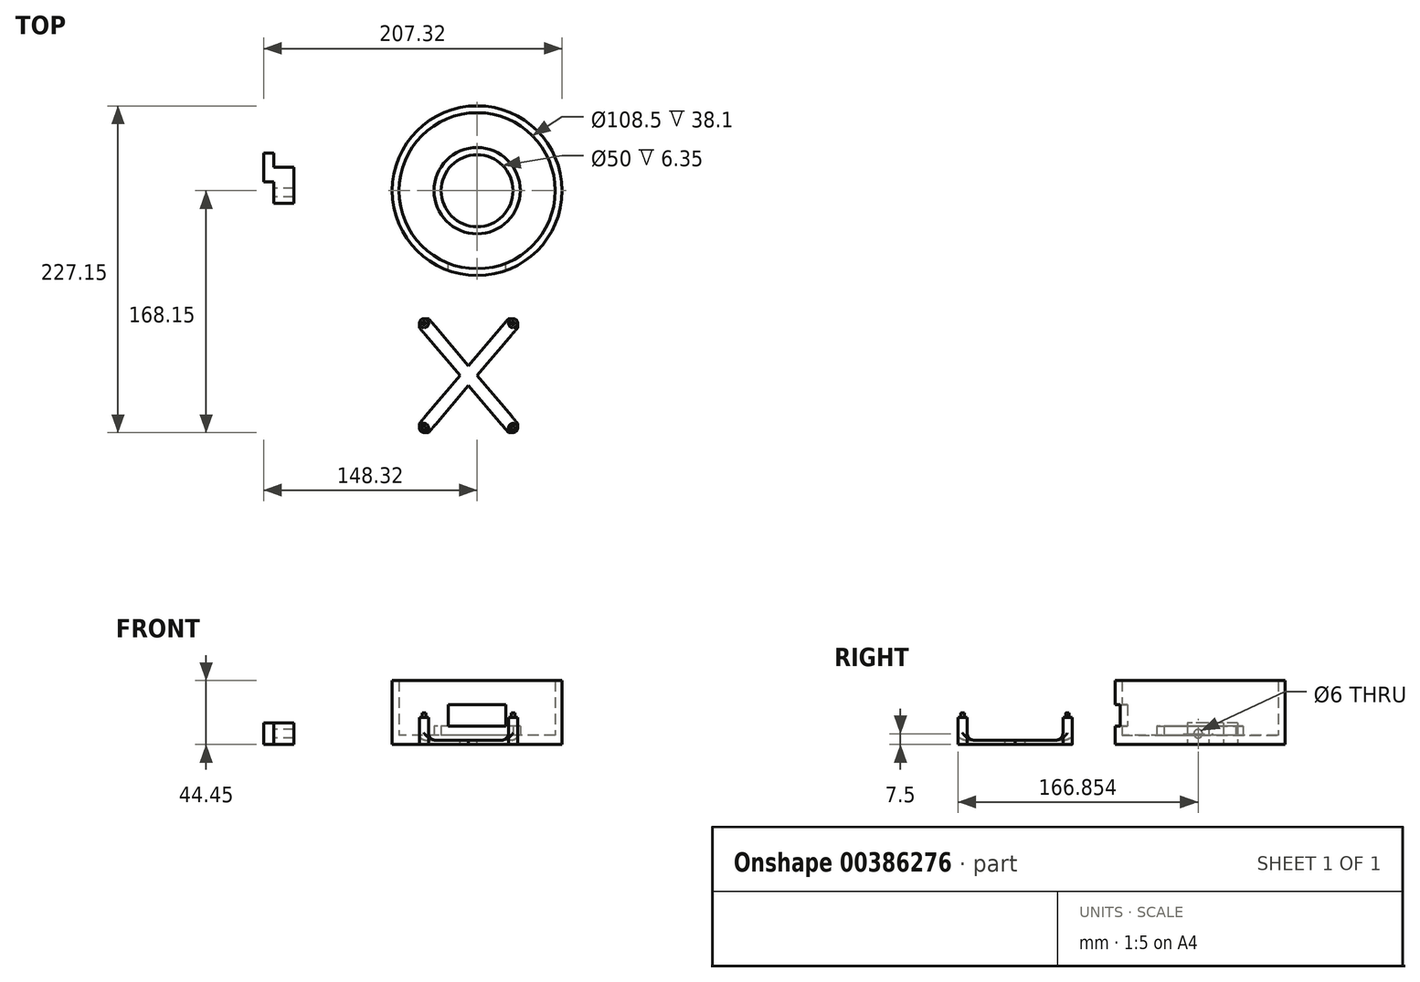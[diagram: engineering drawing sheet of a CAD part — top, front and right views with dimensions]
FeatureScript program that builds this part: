
annotation { "Feature Type Name" : "Feature", "Feature Type Description" : "" }
export const myFeature = defineFeature(function(context is Context, id is Id, definition is map)
    precondition{}
    {
        {
            var Q0;
            Q0=qCreatedBy(makeId("Top.planeOp"),FACE);
            var sketch = newSketch(context, id + "F0", { "sketchPlane" : qUnion([Q0])});
            skCircle(sketch, "E0", {"center": v(0, 0) * mm, "radius": 59 * mm});
            skSolve(sketch);
        }
        {
            var Q0;
            Q0 = qSketchRegion(id + "F0", true);
            extrude(context, id + "F1", {"entities" : qUnion([Q0]), "depth" : 6.35 * mm});
        }
        {
            var Q0;
            Q0=makeQuery(id+"F1.opExtrude","CAP_FACE",FACE,{"disambiguationData":[OSD([sQuery(id+"F0.wireOp",EDGE,"E0")])],"isStart":false});
            var sketch = newSketch(context, id + "F2", { "sketchPlane" : qUnion([Q0])});
            skCircle(sketch, "E1", {"center": v(0, 0) * mm, "radius": 59 * mm});
            skCircle(sketch, "E2", {"center": v(0, 0) * mm, "radius": 54.25 * mm});
            skSolve(sketch);
        }
        {
            var Q0;
            Q0 = qSketchRegion(id + "F2", true);
            extrude(context, id + "F3", {"entities" : qUnion([Q0]), "operationType" : NewBodyOperationType.ADD, "depth" : 38.1 * mm});
        }
        {
            var Q0;
            Q0=makeQuery(id+"F1.opExtrude","CAP_FACE",FACE,{"disambiguationData":[OSD([sQuery(id+"F0.wireOp",EDGE,"E0")])],"isStart":false});
            var sketch = newSketch(context, id + "F4", { "sketchPlane" : qUnion([Q0])});
            skCircle(sketch, "E3", {"center": v(0, 0) * mm, "radius": 30 * mm});
            skCircle(sketch, "E4", {"center": v(0, 0) * mm, "radius": 25 * mm});
            skSolve(sketch);
        }
        {
            var Q0;
            Q0 = qSketchRegion(id + "F4", true);
            extrude(context, id + "F5", {"entities" : qUnion([Q0]), "operationType" : NewBodyOperationType.ADD, "depth" : 6.35 * mm});
        }
        {
            var Q0;
            Q0=qCreatedBy(makeId("Right.planeOp"),FACE);
            var sketch = newSketch(context, id + "F6", { "sketchPlane" : qUnion([Q0])});
            skLineSegment(sketch, "E5.bottom", {"start": v(-62.74, 12.7) * mm, "end": v(-45.16, 12.7) * mm});
            skLineSegment(sketch, "E5.top", {"start": v(-62.74, 27.7) * mm, "end": v(-45.16, 27.7) * mm});
            skLineSegment(sketch, "E5.left", {"start": v(-62.74, 12.7) * mm, "end": v(-62.74, 27.7) * mm});
            skLineSegment(sketch, "E5.right", {"start": v(-45.16, 12.7) * mm, "end": v(-45.16, 27.7) * mm});
            skSolve(sketch);
        }
        {
            var Q0;
            Q0 = qSketchRegion(id + "F6", true);
            extrude(context, id + "F7", {"entities" : qUnion([Q0]), "operationType" : NewBodyOperationType.REMOVE, "depth" : 20 * mm, "hasSecondDirection" : true, "secondDirectionOppositeDirection" : true, "secondDirectionDepth" : 20 * mm, "offsetDistance" : 25 * mm});
        }
        {
            var Q0;
            Q0=qCreatedBy(makeId("Top.planeOp"),FACE);
            var sketch = newSketch(context, id + "F8", { "sketchPlane" : qUnion([Q0])});
            skLineSegment(sketch, "E6.bottom", {"start": v(28.17, -88.95) * mm, "end": v(-40.1, -88.95) * mm});
            skLineSegment(sketch, "E6.top", {"start": v(28.17, -168.15) * mm, "end": v(-40.1, -168.15) * mm});
            skLineSegment(sketch, "E6.left", {"start": v(28.17, -88.95) * mm, "end": v(28.17, -168.15) * mm});
            skLineSegment(sketch, "E6.right", {"start": v(-40.1, -88.95) * mm, "end": v(-40.1, -168.15) * mm});
            skSolve(sketch);
        }
        {
            var Q0;
            Q0 = qSketchRegion(id + "F8", true);
            extrude(context, id + "F9", {"entities" : qUnion([Q0]), "depth" : 3 * mm});
        }
        {
            var Q0;
            Q0=makeQuery(id+"F9.opExtrude","CAP_FACE",FACE,{"disambiguationData":[OSD([sQuery(id+"F8.wireOp",EDGE,"E6.bottom"),sQuery(id+"F8.wireOp",EDGE,"E6.top"),sQuery(id+"F8.wireOp",EDGE,"E6.left"),sQuery(id+"F8.wireOp",EDGE,"E6.right")])],"isStart":false});
            var sketch = newSketch(context, id + "F10", { "sketchPlane" : qUnion([Q0])});
            skPoint(sketch, "E7.centerSnap0", {"position": v(-5.96, -88.95) * mm});
            skPoint(sketch, "E7.centerSnap1", {"position": v(-40.1, -128.55) * mm});
            skLineSegment(sketch, "E8", {"start": v(28.17, -168.15) * mm, "end": v(28.17, -161.8) * mm});
            skLineSegment(sketch, "E9", {"start": v(28.17, -161.8) * mm, "end": v(-33.74, -88.95) * mm});
            skLineSegment(sketch, "E10", {"start": v(-33.74, -88.95) * mm, "end": v(-40.1, -88.95) * mm});
            skLineSegment(sketch, "E11", {"start": v(-40.1, -95.3) * mm, "end": v(21.82, -168.15) * mm});
            skLineSegment(sketch, "E12", {"start": v(21.82, -168.15) * mm, "end": v(28.17, -168.15) * mm});
            skLineSegment(sketch, "E13", {"start": v(-40.1, -168.15) * mm, "end": v(-33.74, -168.15) * mm});
            skLineSegment(sketch, "E14", {"start": v(-33.74, -168.15) * mm, "end": v(28.17, -95.3) * mm});
            skLineSegment(sketch, "E15", {"start": v(28.17, -95.3) * mm, "end": v(28.17, -88.95) * mm});
            skLineSegment(sketch, "E16", {"start": v(21.82, -88.95) * mm, "end": v(-40.1, -161.8) * mm});
            skLineSegment(sketch, "E17", {"start": v(-40.1, -161.8) * mm, "end": v(-40.1, -168.15) * mm});
            skLineSegment(sketch, "E18", {"start": v(21.82, -88.95) * mm, "end": v(28.17, -88.95) * mm});
            skLineSegment(sketch, "E19", {"start": v(-40.1, -95.3) * mm, "end": v(-40.1, -88.95) * mm});
            skLineSegment(sketch, "E20", {"start": v(-33.74, -88.95) * mm, "end": v(21.82, -88.95) * mm});
            skLineSegment(sketch, "E21", {"start": v(28.17, -95.3) * mm, "end": v(28.17, -161.8) * mm});
            skLineSegment(sketch, "E22", {"start": v(21.82, -168.15) * mm, "end": v(-33.74, -168.15) * mm});
            skSolve(sketch);
        }
        {
            var Q0;
            {var subQ0=sQuery(id+"F10.wireOp",EDGE,"E21");Q0=makeQuery(id+"F10.imprint","IMPRINT",FACE,{"disambiguationData":[TD([[makeQuery(id+"F10.imprint","IMPRINT",EDGE,{"derivedFrom":subQ0}),-1.0]])]});}
            var Q1;
            {var subQ0=sQuery(id+"F10.wireOp",EDGE,"E20");Q1=makeQuery(id+"F10.imprint","IMPRINT",FACE,{"disambiguationData":[TD([[makeQuery(id+"F10.imprint","IMPRINT",EDGE,{"derivedFrom":subQ0}),1.0]])]});}
            var Q2;
            {var subQ0=sQuery(id+"F10.wireOp",EDGE,"E22");Q2=makeQuery(id+"F10.imprint","IMPRINT",FACE,{"disambiguationData":[TD([[makeQuery(id+"F10.imprint","IMPRINT",EDGE,{"derivedFrom":subQ0}),-1.0]])]});}
            var Q3;
            {var subQ0=sQuery(id+"F10.wireOp",EDGE,"E11");var subQ3=sQuery(id+"F10.wireOp",EDGE,"E16");var subQ4=makeQuery(id+"F10.imprint","INTERSECT",VERTEX,{"derivedFrom":[subQ0,subQ3]});Q3=makeQuery(id+"F10.imprint","IMPRINT",FACE,{"disambiguationData":[TD([[makeQuery(id+"F10.imprint","IMPRINT",EDGE,{"disambiguationData":[TD([[subQ4,1.0]])],"derivedFrom":subQ0}),-1.0]])]});}
            extrude(context, id + "F11", {"entities" : qUnion([Q0, Q1, Q2, Q3]), "operationType" : NewBodyOperationType.REMOVE, "oppositeDirection" : true, "depth" : 25 * mm});
        }
        {
            var Q0;
            Q0=makeQuery(id+"F9.opExtrude","CAP_FACE",FACE,{"disambiguationData":[OSD([sQuery(id+"F8.wireOp",EDGE,"E6.bottom"),sQuery(id+"F8.wireOp",EDGE,"E6.top"),sQuery(id+"F8.wireOp",EDGE,"E6.left"),sQuery(id+"F8.wireOp",EDGE,"E6.right")])],"isStart":false});
            var sketch = newSketch(context, id + "F12", { "sketchPlane" : qUnion([Q0])});
            skCircle(sketch, "E23", {"center": v(-36.92, -92.13) * mm, "radius": 3.17 * mm});
            skCircle(sketch, "E24", {"center": v(25, -92.13) * mm, "radius": 3.17 * mm});
            skCircle(sketch, "E25", {"center": v(25, -164.98) * mm, "radius": 3.17 * mm});
            skCircle(sketch, "E26", {"center": v(-36.92, -164.98) * mm, "radius": 3.17 * mm});
            skPoint(sketch, "E26.centerSnap0", {"position": v(28.17, -164.98) * mm});
            skSolve(sketch);
        }
        {
            var Q0;
            Q0 = qSketchRegion(id + "F12", true);
            extrude(context, id + "F13", {"entities" : qUnion([Q0]), "operationType" : NewBodyOperationType.ADD, "depth" : 15.88 * mm});
        }
        {
            var Q0;
            Q0=makeQuery(id+"F9.opExtrude","SWEPT_EDGE",EDGE,{"disambiguationData":[OSD([sQuery(id+"F8.wireOp",EDGE,"E6.top"),sQuery(id+"F8.wireOp",EDGE,"E6.right")])]});
            var Q1;
            Q1=makeQuery(id+"F9.opExtrude","SWEPT_EDGE",EDGE,{"disambiguationData":[OSD([sQuery(id+"F8.wireOp",EDGE,"E6.top"),sQuery(id+"F8.wireOp",EDGE,"E6.left")])]});
            var Q2;
            Q2=makeQuery(id+"F9.opExtrude","SWEPT_EDGE",EDGE,{"disambiguationData":[OSD([sQuery(id+"F8.wireOp",EDGE,"E6.bottom"),sQuery(id+"F8.wireOp",EDGE,"E6.left")])]});
            var Q3;
            Q3=makeQuery(id+"F9.opExtrude","SWEPT_EDGE",EDGE,{"disambiguationData":[OSD([sQuery(id+"F8.wireOp",EDGE,"E6.bottom"),sQuery(id+"F8.wireOp",EDGE,"E6.right")])]});
            fillet(context, id + "F14", {"entities" : qUnion([Q0, Q1, Q2, Q3]), "radius" : 3.17 * mm, "tangentPropagation" : true, "allowEdgeOverflow" : false});
        }
        {
            var Q0;
            Q0=makeQuery(id+"F13.opExtrude","CAP_FACE",FACE,{"disambiguationData":[OSD([sQuery(id+"F12.wireOp",EDGE,"E25")])],"isStart":false});
            var sketch = newSketch(context, id + "F15", { "sketchPlane" : qUnion([Q0])});
            skCircle(sketch, "E27", {"center": v(25, -164.98) * mm, "radius": 1.25 * mm});
            skCircle(sketch, "E28", {"center": v(25, -92.13) * mm, "radius": 1.25 * mm});
            skCircle(sketch, "E29", {"center": v(-36.92, -92.13) * mm, "radius": 1.25 * mm});
            skCircle(sketch, "E30", {"center": v(-36.92, -164.98) * mm, "radius": 1.25 * mm});
            skSolve(sketch);
        }
        {
            var Q0;
            Q0 = qSketchRegion(id + "F15", true);
            extrude(context, id + "F16", {"entities" : qUnion([Q0]), "operationType" : NewBodyOperationType.ADD, "depth" : 3 * mm});
        }
        {
            var Q0;
            Q0=makeQuery(id+"F13.boolean.opBoolean","SPLIT",EDGE,{"disambiguationData":[OD(1.0)],"derivedFrom":makeQuery(id+"F13.opExtrude","CAP_EDGE",EDGE,{"disambiguationData":[OSD([sQuery(id+"F12.wireOp",EDGE,"E25")])],"isStart":true})});
            var Q1;
            Q1=makeQuery(id+"F13.boolean.opBoolean","SPLIT",EDGE,{"disambiguationData":[OD(1.0)],"derivedFrom":makeQuery(id+"F13.opExtrude","CAP_EDGE",EDGE,{"disambiguationData":[OSD([sQuery(id+"F12.wireOp",EDGE,"E26")])],"isStart":true})});
            var Q2;
            Q2=makeQuery(id+"F13.boolean.opBoolean","SPLIT",EDGE,{"disambiguationData":[OD(1.0)],"derivedFrom":makeQuery(id+"F13.opExtrude","CAP_EDGE",EDGE,{"disambiguationData":[OSD([sQuery(id+"F12.wireOp",EDGE,"E24")])],"isStart":true})});
            var Q3;
            Q3=makeQuery(id+"F13.boolean.opBoolean","SPLIT",EDGE,{"disambiguationData":[OD(1.0)],"derivedFrom":makeQuery(id+"F13.opExtrude","CAP_EDGE",EDGE,{"disambiguationData":[OSD([sQuery(id+"F12.wireOp",EDGE,"E23")])],"isStart":true})});
            fillet(context, id + "F17", {"entities" : qUnion([Q0, Q1, Q2, Q3]), "radius" : 5 * mm, "tangentPropagation" : true, "allowEdgeOverflow" : false});
        }
        {
            var Q0;
            Q0=qCreatedBy(makeId("Top.planeOp"),FACE);
            var sketch = newSketch(context, id + "F18", { "sketchPlane" : qUnion([Q0])});
            skLineSegment(sketch, "E31.bottom", {"start": v(-148.32, 26.2) * mm, "end": v(-141.32, 26.2) * mm});
            skLineSegment(sketch, "E31.top", {"start": v(-148.32, 6.2) * mm, "end": v(-141.32, 6.2) * mm});
            skLineSegment(sketch, "E31.left", {"start": v(-148.32, 26.2) * mm, "end": v(-148.32, 6.2) * mm});
            skLineSegment(sketch, "E31.right", {"start": v(-141.32, 26.2) * mm, "end": v(-141.32, 6.2) * mm});
            skLineSegment(sketch, "E32.bottom", {"start": v(-141.32, 16.2) * mm, "end": v(-127.32, 16.2) * mm});
            skLineSegment(sketch, "E32.top", {"start": v(-141.32, -8.8) * mm, "end": v(-127.32, -8.8) * mm});
            skLineSegment(sketch, "E32.left", {"start": v(-141.32, 16.2) * mm, "end": v(-141.32, -8.8) * mm});
            skLineSegment(sketch, "E32.right", {"start": v(-127.32, 16.2) * mm, "end": v(-127.32, -8.8) * mm});
            skSolve(sketch);
        }
        {
            var Q0;
            Q0 = qSketchRegion(id + "F18", true);
            extrude(context, id + "F19", {"entities" : qUnion([Q0]), "depth" : 15 * mm, "offsetDistance" : 25 * mm});
        }
        {
            var Q0;
            Q0=makeQuery(id+"F19.opExtrude","SWEPT_FACE",FACE,{"disambiguationData":[OSD([sQuery(id+"F18.wireOp",EDGE,"E32.left")])]});
            var sketch = newSketch(context, id + "F20", { "sketchPlane" : qUnion([Q0])});
            skCircle(sketch, "E33", {"center": v(1.3, 7.5) * mm, "radius": 3 * mm});
            skPoint(sketch, "E33.centerSnap0", {"position": v(1.3, 15) * mm});
            skPoint(sketch, "E33.centerSnap1", {"position": v(8.8, 7.5) * mm});
            skSolve(sketch);
        }
        {
            var Q0;
            Q0 = qSketchRegion(id + "F20", true);
            extrude(context, id + "F21", {"entities" : qUnion([Q0]), "operationType" : NewBodyOperationType.REMOVE, "oppositeDirection" : true, "depth" : 25 * mm, "offsetDistance" : 25 * mm});
        }
    });
